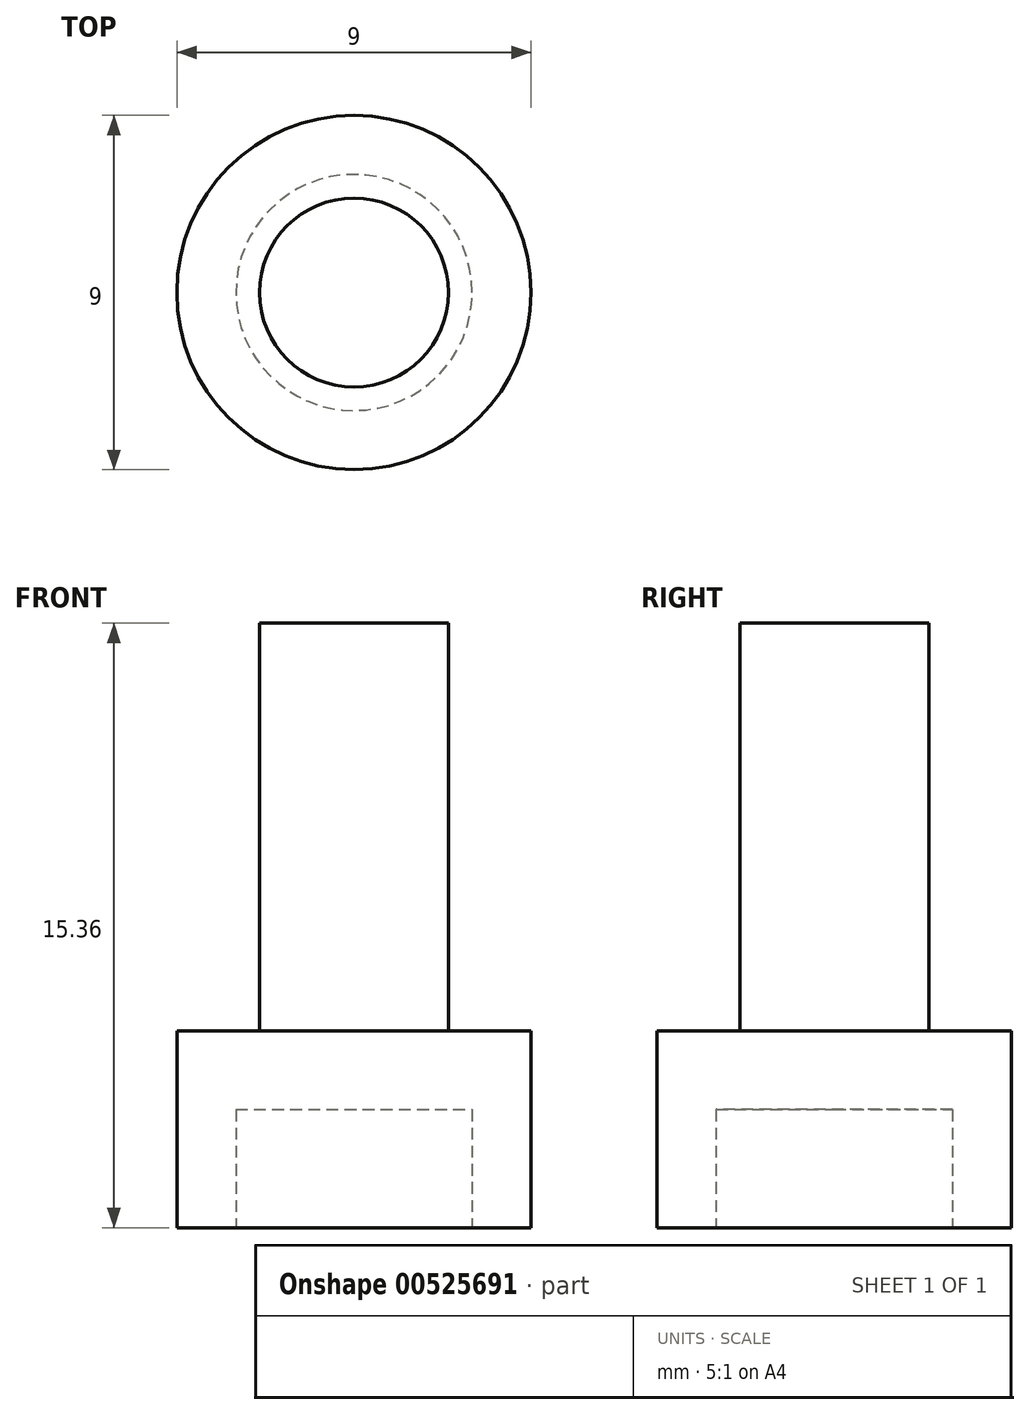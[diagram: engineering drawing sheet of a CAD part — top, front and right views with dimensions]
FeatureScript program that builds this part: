
annotation { "Feature Type Name" : "Feature", "Feature Type Description" : "" }
export const myFeature = defineFeature(function(context is Context, id is Id, definition is map)
    precondition{}
    {
        {
            var Q0;
            Q0=qCreatedBy(makeId("Top.planeOp"),FACE);
            var sketch = newSketch(context, id + "F0", { "sketchPlane" : qUnion([Q0])});
            skCircle(sketch, "E0", {"center": v(0, 0) * mm, "radius": 4.5 * mm});
            skCircle(sketch, "E1", {"center": v(0, 0) * mm, "radius": 2.4 * mm});
            skSolve(sketch);
        }
        {
            var Q0;
            Q0=makeQuery(id+"F0.imprint","IMPRINT",FACE,{"disambiguationData":[TD([[makeQuery(id+"F0.imprint","IMPRINT",EDGE,{"derivedFrom":sQuery(id+"F0.wireOp",EDGE,"E1")}),1.0]])]});
            extrude(context, id + "F1", {"entities" : qUnion([Q0]), "depth" : 10.36 * mm, "offsetDistance" : 25 * mm});
        }
        {
            var Q0;
            Q0 = qSketchRegion(id + "F0", true);
            var Q1;
            Q1=makeQuery(id+"F1.opExtrude","CAP_FACE",FACE,{"disambiguationData":[OSD([sQuery(id+"F0.wireOp",EDGE,"E1")])],"isStart":true});
            extrude(context, id + "F2", {"entities" : qUnion([Q0, Q1]), "operationType" : NewBodyOperationType.ADD, "oppositeDirection" : true, "depth" : 5 * mm, "offsetDistance" : 25 * mm});
        }
        {
            var Q0;
            {var subQ0=sQuery(id+"F0.wireOp",EDGE,"E1");Q0=makeQuery(id+"F2.boolean.opBoolean","MERGE",FACE,{"derivedFrom":[makeQuery(id+"F2.opExtrude","CAP_FACE",FACE,{"disambiguationData":[OSD([sQuery(id+"F0.wireOp",EDGE,"E0"),subQ0])],"isStart":false}),makeQuery(id+"F2.opExtrude","CAP_FACE",FACE,{"disambiguationData":[OSD([subQ0])],"isStart":false})]});}
            var sketch = newSketch(context, id + "F3", { "sketchPlane" : qUnion([Q0])});
            skCircle(sketch, "E2", {"center": v(0, 0) * mm, "radius": 3 * mm});
            skSolve(sketch);
        }
        {
            var Q0;
            Q0=makeQuery(id+"F3.imprint","IMPRINT",FACE,{"disambiguationData":[TD([[makeQuery(id+"F3.imprint","IMPRINT",EDGE,{"derivedFrom":sQuery(id+"F3.wireOp",EDGE,"E2")}),1.0]])]});
            extrude(context, id + "F4", {"entities" : qUnion([Q0]), "operationType" : NewBodyOperationType.REMOVE, "oppositeDirection" : true, "depth" : 3 * mm, "offsetDistance" : 25 * mm});
        }
    });
